# Revit family: Zumtobel TECTON 2 continuous row element ECOOS 2
name_source: partatom
category: Lighting Fixtures
units: mm (PartAtom-declared; Revit-internal decimal feet)

## family parameters
Cut with Voids When Loaded = No
Host = Face
Light Source = Yes
Maintain Annotation Orientation = No
Part Type = Normal
Room Calculation Point = Yes
Round Connector Dimension = Use Diameter
Shared = No

## types (1)
- Zumtobel TECTON 2 continuous row element ECOOS 2
    Apparent Load = 35 VA
    Assembly Code = Pr_70_70_48_19
    Color Filter = 16777215
    Default Elevation = 0 mm  [stored 0 ft]
    Description = Continuous-row Lighting Luminaires
    Dimming Lamp Color Temperature Shift = <None>
    Emit Shape Visible in Rendering = No
    Emit from Rectangle Length = 120 mm  [stored 0.393701 ft]
    Emit from Rectangle Width = 1238 mm  [stored 4.06168 ft]
    Export Type to IFC As = IfcLightFixtureType
    Housing L12 = Yes
    Housing L15 = No
    Housing Slim = No
    Lamp = LED
    Luminaire Height = 73.81 mm  [stored 0.242159 ft]
    Luminaire Length = 1264 mm  [stored 4.14698 ft]
    Luminaire Width = 120 mm  [stored 0.393701 ft]
    Manufacturer = Zumtobel Lighting
    Model = 42191044
    Photometric Web File = 42191044_(STD_LEO).IES
    Power Factor = 0.94
    TECTON 2 Adapter Length = 1251 mm  [stored 4.10433 ft]
    Tilt Angle = -90.00°
    Type IFC Predefined Type = DIRECTIONSOURCE
    Type Image = ZS_TE2_F_ECOOS2_stnd_config_WH.jpg
    URL = https://www.zumtobel.com

note: [stored X ft] marks values corroborated as IEEE doubles in the binary element streams (Revit-internal decimal feet)

## geometry (parser evidence)
native form markers: Sweep x7
no freeform markers — native parametric forms only
